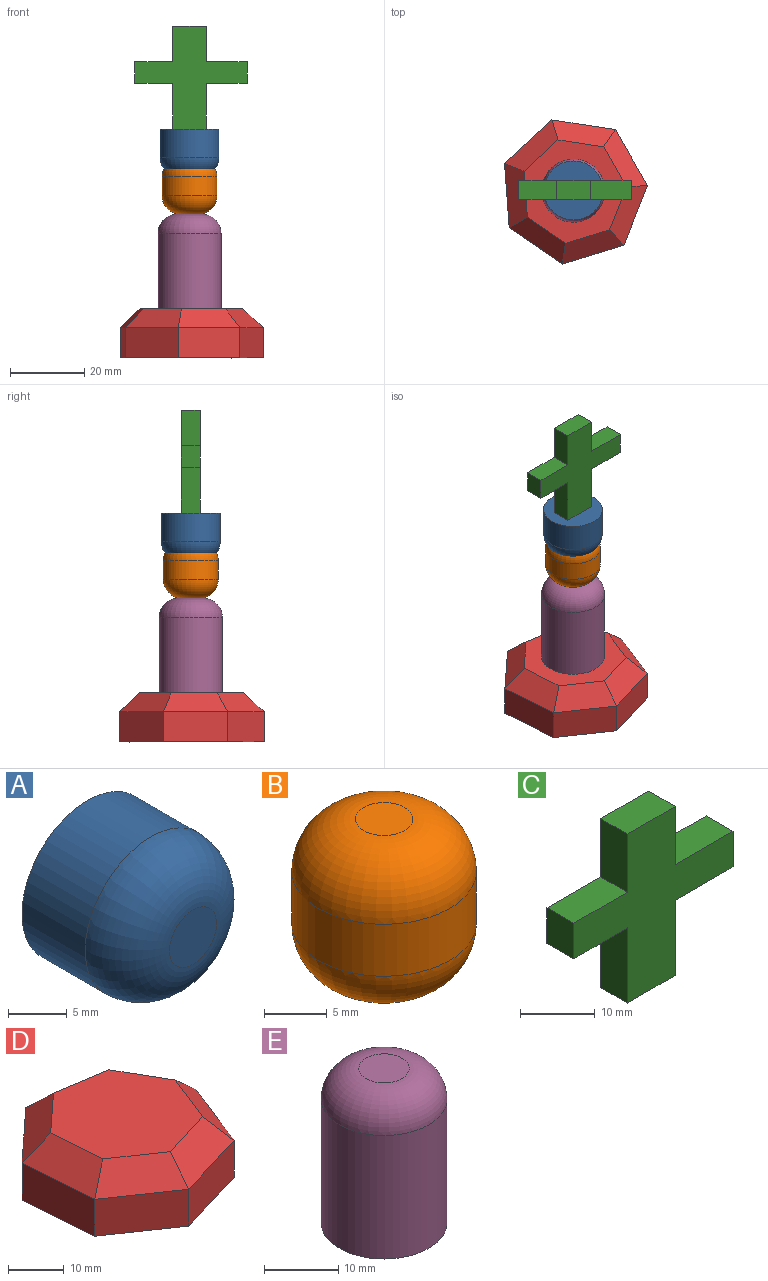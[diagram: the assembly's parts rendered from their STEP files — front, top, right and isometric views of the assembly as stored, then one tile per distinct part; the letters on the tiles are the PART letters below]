
ASSEMBLY  parts=5 mates=4
PART A: 4 faces, bbox 15.8x12.7x15.8 mm
  f0: cylinder r=7.92mm len=15.83mm, axis (0,1,0), area 379mm2, adj f2,f3
  f1: plane 5.67x5.67mm, normal (0,-1,0), area 25.3mm2, adj f3
  f2: plane 15.83x15.83mm, normal (0,1,0), area 196.9mm2, adj f0
  f3: torus R=2.84mm, axis (0,-1,0), area 304.4mm2, adj f0,f1
PART B: 5 faces, bbox 14.7x14.7x15.2 mm
  f0: cylinder r=7.36mm len=14.73mm, axis (0,0,-1), area 235mm2, adj f3,f4
  f1: plane 4.57x4.57mm, normal (0,0,1), area 16.4mm2, adj f4
  f2: plane 4.57x4.57mm, normal (0,0,-1), area 16.4mm2, adj f3
  f3: torus R=2.28mm, axis (0,0,1), area 276.6mm2, adj f0,f2
  f4: torus R=2.28mm, axis (0,0,1), area 276.6mm2, adj f0,f1
PART C: 14 faces, bbox 30.2x5.1x27.7 mm
  f0: plane 9.56x5.08mm, normal (-1,0,0), area 48.6mm2, adj f1,f11,f12,f13
  f1: plane 10.17x5.08mm, normal (0,0,1), area 51.7mm2, adj f0,f2,f12,f13
  f2: plane 5.86x5.08mm, normal (-1,0,0), area 29.8mm2, adj f1,f3,f12,f13
  f3: plane 10.17x5.08mm, normal (0,0,-1), area 51.7mm2, adj f2,f4,f12,f13
  f4: plane 12.33x5.08mm, normal (-1,0,0), area 62.7mm2, adj f3,f5,f12,f13
  f5: plane 9.1x5.08mm, normal (0,0,-1), area 46.2mm2, adj f4,f6,f12,f13
  f6: plane 12.33x5.08mm, normal (1,0,0), area 62.7mm2, adj f5,f7,f12,f13
  f7: plane 10.95x5.08mm, normal (0,0,-1), area 55.6mm2, adj f6,f8,f12,f13
  f8: plane 5.86x5.08mm, normal (1,0,0), area 29.8mm2, adj f7,f9,f12,f13
  f9: plane 10.95x5.08mm, normal (0,0,1), area 55.6mm2, adj f8,f10,f12,f13
  f10: plane 9.56x5.08mm, normal (1,0,0), area 48.6mm2, adj f9,f11,f12,f13
  f11: plane 9.1x5.08mm, normal (0,0,1), area 46.2mm2, adj f0,f10,f12,f13
  f12: plane 30.22x27.75mm, normal (0,-1,0), area 376.1mm2, adj f0,f1,f2,f3,f4,f5,f6,f7
  f13: plane 30.22x27.75mm, normal (0,1,0), area 376.1mm2, adj f0,f1,f2,f3,f4,f5,f6,f7
PART D: 16 faces, bbox 38.4x38.8x13.2 mm
  f0: plane 15x8.61mm, normal (0.87,0.5,0), area 140.6mm2, adj f1,f6,f8,f14
  f1: plane 17.09x8.13mm, normal (0.15,0.99,0), area 140.6mm2, adj f0,f2,f8,f15
  f2: plane 12.7x11.73mm, normal (-0.68,0.73,0), area 140.6mm2, adj f1,f3,f8,f13
  f3: plane 17.25x8.13mm, normal (-1,-0.07,0), area 140.6mm2, adj f2,f4,f8,f11
  f4: plane 14.27x9.78mm, normal (-0.57,-0.82,0), area 140.6mm2, adj f3,f5,f8,f9
  f5: plane 16.54x8.13mm, normal (0.29,-0.96,0), area 140.6mm2, adj f4,f6,f8,f10
  f6: plane 16.08x8.13mm, normal (0.93,-0.37,0), area 140.6mm2, adj f0,f5,f8,f12
  f7: plane 27.79x27.54mm, normal (0,0,1), area 558.8mm2, adj f9,f10,f11,f12,f13,f14,f15
  f8: plane 38.76x38.41mm, normal (0,0,-1), area 1086.8mm2, adj f0,f1,f2,f3,f4,f5,f6
  f9: plane 15.12x12.58mm, normal (-0.4,-0.58,0.71), area 106.7mm2, adj f4,f7,f10,f11
  f10: plane 16.54x9.2mm, normal (0.21,-0.68,0.71), area 106.7mm2, adj f5,f7,f9,f12
  f11: plane 17.25x6.14mm, normal (-0.71,-0.05,0.71), area 106.7mm2, adj f3,f7,f9,f13
  f12: plane 16.08x10.18mm, normal (0.66,-0.26,0.71), area 106.7mm2, adj f6,f7,f10,f14
  f13: plane 14.35x13.81mm, normal (-0.48,0.52,0.71), area 106.7mm2, adj f2,f7,f11,f15
  f14: plane 15.41x11.8mm, normal (0.61,0.35,0.71), area 106.7mm2, adj f0,f7,f12,f15
  f15: plane 17.09x7.27mm, normal (0.11,0.7,0.71), area 106.7mm2, adj f1,f7,f13,f14
PART E: 4 faces, bbox 16.9x16.9x25.4 mm
  f0: cylinder r=8.47mm len=20.32mm, axis (0,0,-1), area 1080.9mm2, adj f2,f3
  f1: plane 6.77x6.77mm, normal (0,0,1), area 36mm2, adj f3
  f2: plane 16.93x16.93mm, normal (0,0,-1), area 225.2mm2, adj f0
  f3: torus R=3.39mm, axis (0,0,1), area 331.9mm2, adj f0,f1
PLACE A rot(axis=(1,0,0),90deg) t=(14.84,1.02,27.63)mm
PLACE B t=(14.84,1.02,4.77)mm
PLACE C t=(19.38,3.56,27.63)mm
PLACE D t=(14.84,1.02,-33.84)mm
PLACE E t=(12.22,1.02,-20.63)mm
MATE fastened B.f0 <-> E.f0  axis (0,0,-1) through (14.84,1.02,4.77)mm
MATE fastened E.f0 <-> D.f7  axis (0,0,-1) through (14.84,1.02,-20.63)mm
MATE fastened C.f5 <-> A.f0  axis (0,0,-1) through (14.84,1.02,27.63)mm
MATE fastened A.f0 <-> B.f0  axis (0,0,1) through (14.84,1.02,20.01)mm
